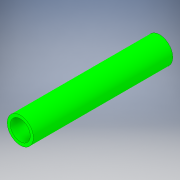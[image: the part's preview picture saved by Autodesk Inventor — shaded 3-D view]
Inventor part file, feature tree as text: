
AUTODESK INVENTOR PART (.ipt)
format: ipt  version: 2018 (Build 220112000, 112)  size: 108,032 bytes
history: native  units: in
note: dims shown in document units (in); Inventor stores cm internally (conversion verified against a paired STEP export)
features: extrude x1, sketch x1
ambient origin geometry x8: Origin, YZ Plane, XZ Plane, XY Plane, X Axis, Y Axis, Z Axis, Center Point
bodies: Solid1 (feature_tree)
feature tree (2):
  extrude  "Extrusion1"  Depth=7.0in
  sketch  "Sketch1"  dims[d0=1.315in d1=1.0in d2=7.0in d3=0.0in]
